# Revit family: Gaius Cabinet Tall_
name_source: partatom
category: Casework
revit_build: Autodesk Revit Architecture 2012 (Build: 20110916_2132(x64)
units: mm (PartAtom-declared; Revit-internal decimal feet)

## types (4) — shared parameters
Body Material = Laminate White
Door Edge Color = Laminate Grey
Door Material = Laminate White
Manufacturer = Korpinen Oy
URL = www.korpinen.com
zero-valued in all types: Depth, Height

## per-type parameters (varying)
| type | Handrail Color | Model | Type Comments | Width |
| 6300 | RAL 3003 - Red | 6300 Gaius Cabinet |  | 400 mm  [stored 1.31234 ft] |
| 6301 | <By Category> | 6301 Gaius Cabinet |  | 400 mm  [stored 1.31234 ft] |
| 6305 | <By Category> | 6305 Gaius Cabinet | Cleaning Cabinet | 0 mm  [stored 0 ft] |
| 6308 | RAL 3003 - Red | 6308 Gaius Cabinet | Cabinet with Handrail | 400 mm  [stored 1.31234 ft] |

note: column(s) folded — value = type name in every type: Cabinet Type

note: [stored X ft] marks values corroborated as IEEE doubles in the binary element streams (Revit-internal decimal feet)

## geometry (parser evidence)
native form markers: Sweep x31
no freeform markers — native parametric forms only
